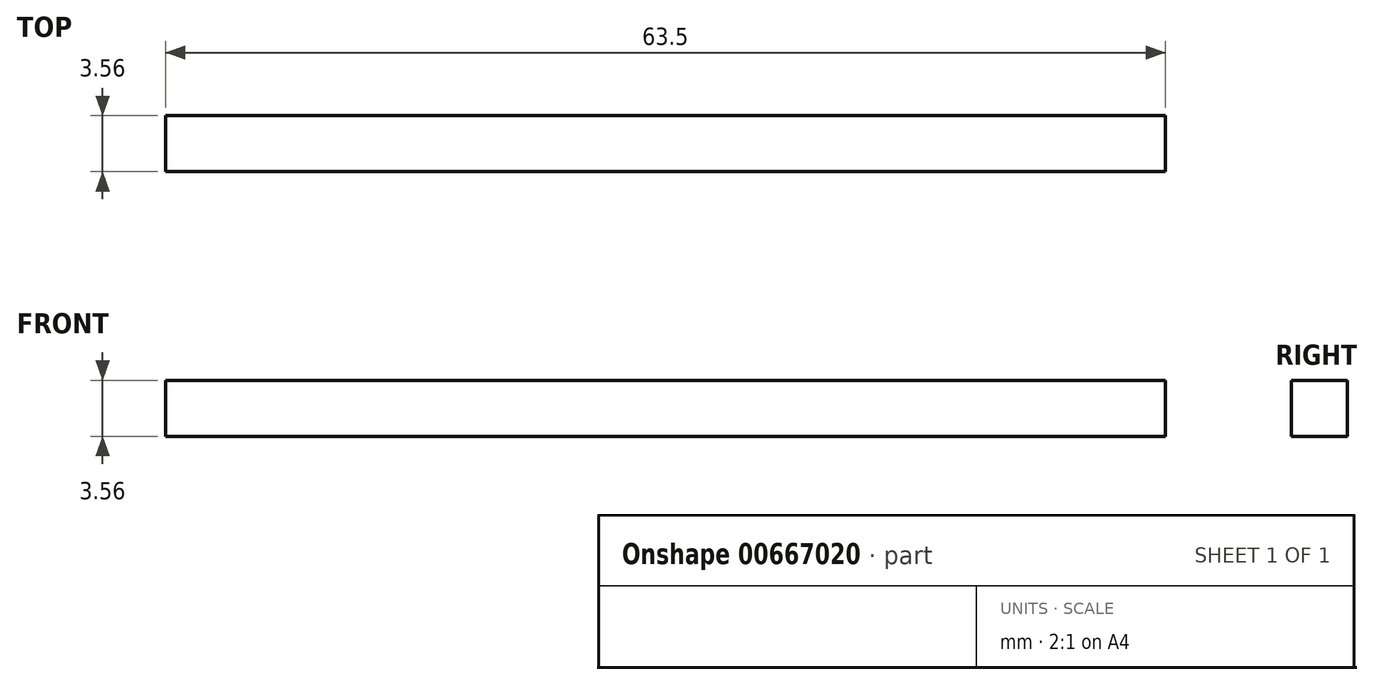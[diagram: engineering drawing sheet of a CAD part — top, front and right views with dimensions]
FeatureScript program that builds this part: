
annotation { "Feature Type Name" : "Feature", "Feature Type Description" : "" }
export const myFeature = defineFeature(function(context is Context, id is Id, definition is map)
    precondition{}
    {
        {
            var Q0;
            Q0=qCreatedBy(makeId("Front.planeOp"),FACE);
            var sketch = newSketch(context, id + "F0", { "sketchPlane" : qUnion([Q0])});
            skLineSegment(sketch, "E0", {"start": v(214.55, 8.42) * mm, "end": v(278.05, 8.42) * mm});
            skLineSegment(sketch, "E1", {"start": v(214.55, 8.42) * mm, "end": v(214.55, 11.98) * mm});
            skLineSegment(sketch, "E2", {"start": v(214.55, 11.98) * mm, "end": v(278.05, 11.98) * mm});
            skLineSegment(sketch, "E3", {"start": v(278.05, 11.98) * mm, "end": v(278.05, 8.42) * mm});
            skSolve(sketch);
        }
        {
            var Q0;
            Q0 = qSketchRegion(id + "F0", true);
            extrude(context, id + "F1", {"entities" : qUnion([Q0]), "depth" : 3.56 * mm, "offsetDistance" : 25.4 * mm});
        }
    });
